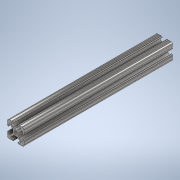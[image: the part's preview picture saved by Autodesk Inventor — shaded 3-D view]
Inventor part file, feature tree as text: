
AUTODESK INVENTOR PART (.ipt)
format: ipt  version: 2020 (Build 240168000, 168)  size: 239,104 bytes
history: native  units: in
note: dims shown in document units (in); Inventor stores cm internally (conversion verified against a paired STEP export)
features: extrude x1, sketch x1
ambient origin geometry x8: Origin, YZ Plane, XZ Plane, XY Plane, X Axis, Y Axis, Z Axis, Center Point
bodies: Solid1 (feature_tree)
feature tree (2):
  extrude  "Extrusion1"  [1 undecoded]
  sketch  "Sketch1"  dims[d0=9.0in d1=0.0in]
note: 1 required parameter value undecoded (feature->parameter linkage not recoverable at this tier; creation-order binding heuristic only, values carry confidence <= 0.55)
